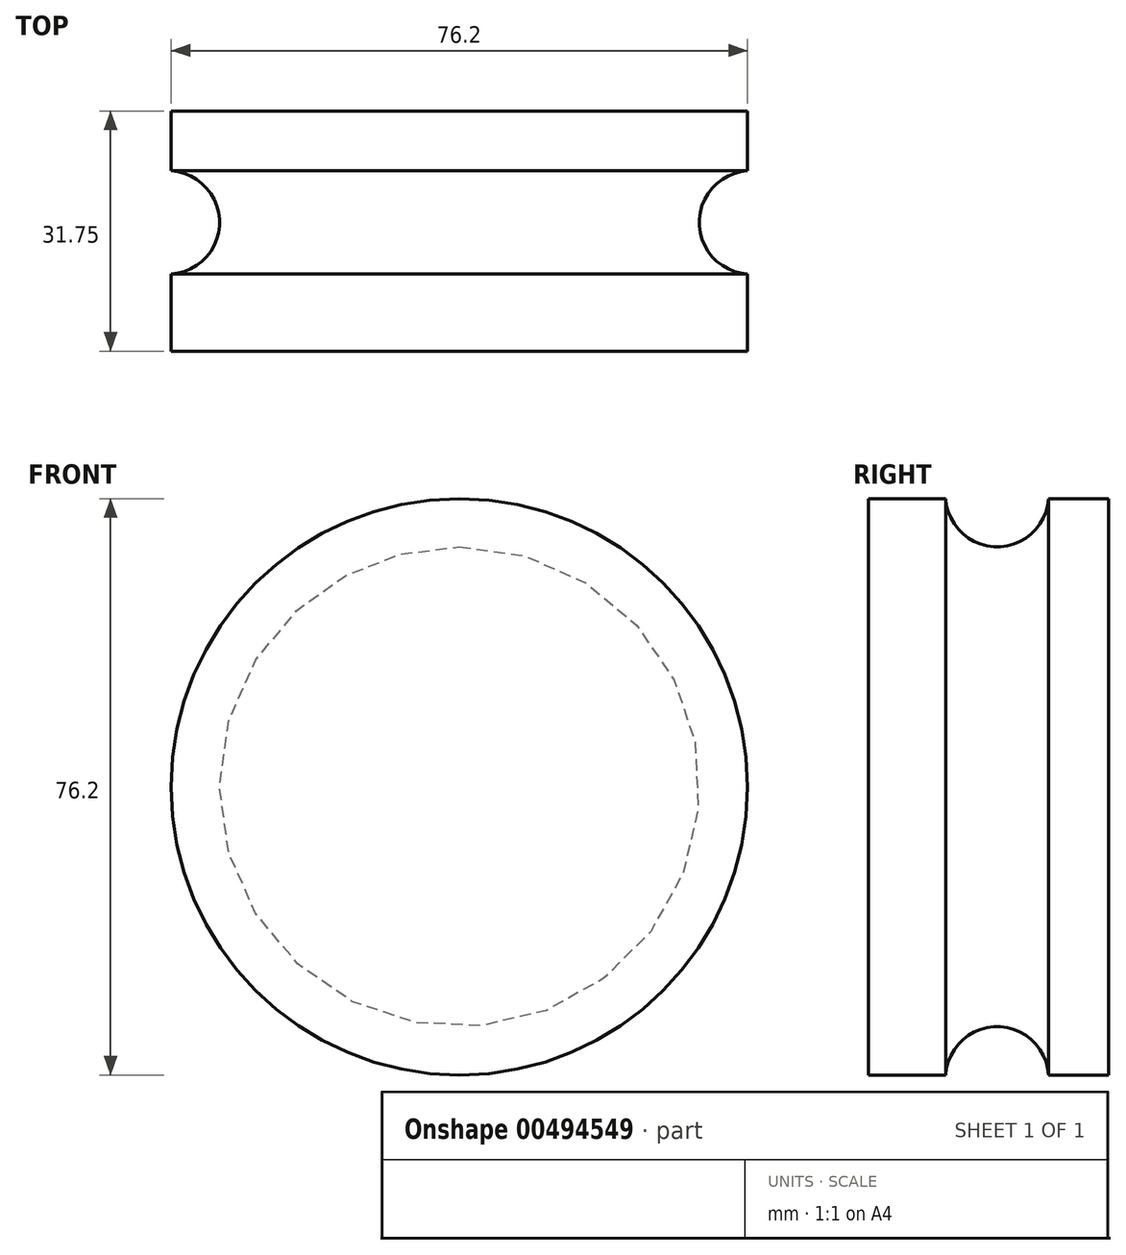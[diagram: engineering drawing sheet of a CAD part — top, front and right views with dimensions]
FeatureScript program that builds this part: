
annotation { "Feature Type Name" : "Feature", "Feature Type Description" : "" }
export const myFeature = defineFeature(function(context is Context, id is Id, definition is map)
    precondition{}
    {
        {
            var Q0;
            Q0=qCreatedBy(makeId("Front.planeOp"),FACE);
            var sketch = newSketch(context, id + "F0", { "sketchPlane" : qUnion([Q0])});
            skCircle(sketch, "E0", {"center": v(0, 0) * mm, "radius": 38.1 * mm});
            skSolve(sketch);
        }
        {
            var Q0;
            Q0=makeQuery(id+"F0.imprint","IMPRINT",FACE,{"disambiguationData":[TD([[makeQuery(id+"F0.imprint","IMPRINT",EDGE,{"derivedFrom":sQuery(id+"F0.wireOp",EDGE,"E0")}),1.0]])]});
            extrude(context, id + "F1", {"entities" : qUnion([Q0]), "depth" : 31.75 * mm});
        }
        {
            var Q0;
            Q0=qCreatedBy(makeId("Top.planeOp"),FACE);
            var sketch = newSketch(context, id + "F2", { "sketchPlane" : qUnion([Q0])});
            skCircle(sketch, "E1", {"center": v(38.55, -14.75) * mm, "radius": 6.83 * mm});
            skSolve(sketch);
        }
        {
            var Q0;
            Q0=makeQuery(id+"F2.imprint","IMPRINT",FACE,{"disambiguationData":[TD([[makeQuery(id+"F2.imprint","IMPRINT",EDGE,{"derivedFrom":sQuery(id+"F2.wireOp",EDGE,"E1")}),1.0]])]});
            var Q1;
            Q1=makeQuery(id+"F1.opExtrude","CAP_EDGE",EDGE,{"disambiguationData":[OSD([sQuery(id+"F0.wireOp",EDGE,"E0")])],"isStart":false});
            revolve(context, id + "F3", {"operationType" : NewBodyOperationType.REMOVE, "entities" : qUnion([Q0]), "axis" : qUnion([Q1]), "revolveType" : RevolveType.FULL});
        }
    });
